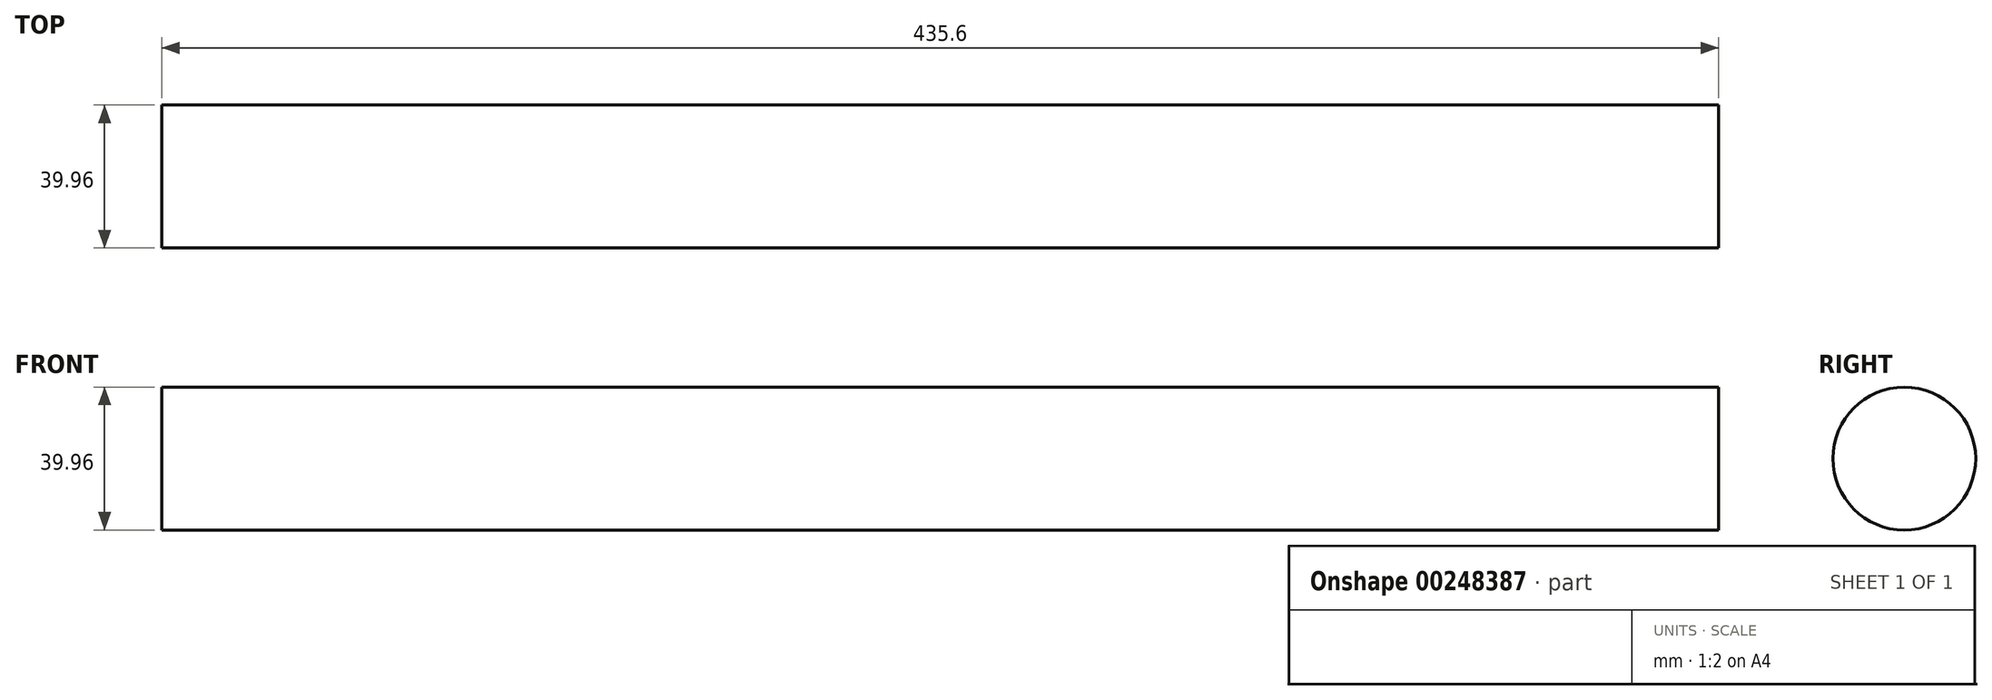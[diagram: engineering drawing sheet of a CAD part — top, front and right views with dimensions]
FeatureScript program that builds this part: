
annotation { "Feature Type Name" : "Feature", "Feature Type Description" : "" }
export const myFeature = defineFeature(function(context is Context, id is Id, definition is map)
    precondition{}
    {
        {
            var Q0;
            Q0=qCreatedBy(makeId("Right.planeOp"),FACE);
            var sketch = newSketch(context, id + "F0", { "sketchPlane" : qUnion([Q0])});
            skCircle(sketch, "E0", {"center": v(0, 0) * mm, "radius": 19.98 * mm});
            skSolve(sketch);
        }
        {
            var Q0;
            Q0=makeQuery(id+"F0.imprint","IMPRINT",FACE,{"disambiguationData":[TD([[makeQuery(id+"F0.imprint","IMPRINT",EDGE,{"derivedFrom":sQuery(id+"F0.wireOp",EDGE,"E0")}),1.0]])]});
            extrude(context, id + "F1", {"entities" : qUnion([Q0]), "depth" : 435.6 * mm});
        }
    });
